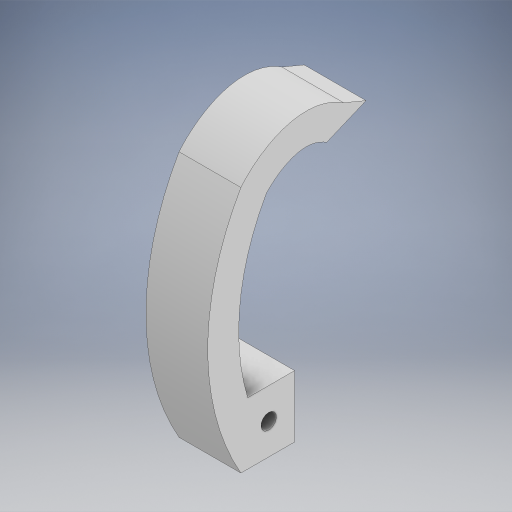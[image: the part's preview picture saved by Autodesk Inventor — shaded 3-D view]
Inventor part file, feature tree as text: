
AUTODESK INVENTOR PART (.ipt)
format: ipt  version: 2024.2 (Build 282272000, 272)  size: 276,480 bytes
history: native  units: in
note: dims shown in document units (in); Inventor stores cm internally (conversion verified against a paired STEP export)
features: extrude x1, sketch x1
ambient origin geometry x8: Origin, YZ Plane, XZ Plane, XY Plane, X Axis, Y Axis, Z Axis, Center Point
bodies: Solid1 (feature_tree)
feature tree (2):
  extrude  "Extrusion1"  Depth=1.0in TaperAngle=0.0deg
  sketch  "Sketch1"  dims[d0=4.0in d1=4.0in d2=0.5in d3=1.0in d4=0.0in]
